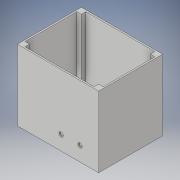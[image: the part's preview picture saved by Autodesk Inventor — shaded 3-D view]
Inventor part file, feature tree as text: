
AUTODESK INVENTOR PART (.ipt)
format: ipt  version: 2018 (Build 220112000, 112)  size: 168,448 bytes
history: native  units: in
note: dims shown in document units (in); Inventor stores cm internally (conversion verified against a paired STEP export)
features: extrude x6, sketch x6
ambient origin geometry x8: Origin, YZ Plane, XZ Plane, XY Plane, X Axis, Y Axis, Z Axis, Center Point
bodies: Solid1 (feature_tree)
feature tree (12):
  extrude  "Extrusion1"  Depth=3.701in
  extrude  "Extrusion2"  Depth=4.527in
  extrude  "Extrusion3"  Depth=0.354in
  extrude  "Extrusion6"  Depth=0.354in
  extrude  "Extrusion7"  Depth=4.0in TaperAngle=0.0deg
  extrude  "Extrusion8"  Depth=0.164in
  sketch  "Sketch1"  dims[d0=4.705in d1=3.701in]
  sketch  "Sketch2"  dims[d2=0.089in d3=0.0in d4=4.527in]
  sketch  "Sketch3"  dims[d5=3.523in d6=0.354in]
  sketch  "Sketch7"  dims[d7=0.354in d10=0.354in]
  sketch  "Sketch8"  dims[d11=0.354in d14=4.0in d15=0.0in]
  sketch  "Sketch9"  dims[d18=0.164in d19=0.164in d20=0.0in d21=0.0in d57=0.112in d58=0.112in d59=0.112in d60=0.112in d61=2.598in d62=0.787in d63=0.118in d64=0.118in d65=0.118in d66=0.118in d67=0.0in d68=0.0in d71=0.25in d72=0.25in d73=0.0in d74=0.0in d79=0.25in d80=0.25in d81=0.0in d82=0.0in]
